# Revit family: 63 T Schraubflansch
name_source: partatom
category: Instalační zařizovací předměty
revit_build: Autodesk Revit 2016 (Build: 20161004_0715(x64)
units: mm (PartAtom-declared; Revit-internal decimal feet)

## family parameters
Bod výpočtu místnosti = Ano
Kóta kulaté spojky = Použít průměr
Nadpis OmniClass = Deck Waste Water Drains
Ořezat dutým tvarem při načtení = Ne
Sdílené = Ne
Typ součásti = Normální
Vždy vertikální = Ano
Založené na pracovní rovině = Ne
Číslo OmniClass = 23.70.50.21.24.14

## types (4) — shared parameters
BUILD-IN HEIGHT = 300 mm
Klíčová poznámka = 63 T Schraubflansch
MATERIAL = PP, TPE
Model = 63 T Schraubflansch
Popis = Roof drains
Připojení CW = Ne
Připojení HW = Ne
Připojení odpadu = Ano
Připojení ventilace = Ne
URL = http://www.dallmer.com
Výrobce = Dallmer Ltd.

## per-type parameters (varying)
| type | CAPACITY | DIMENSION | GTIN | Komentáře k typům | NOMINAL DIAMETER | WEIGHT |
| 63 T Schraubflansch.0049 | 9,7 | DN 70 | 4001636630049 | renova roof drain type 63 T clamp ring, 345 mm, DN 70 | 70 mm | 2,22 |
| 63 T Schraubflansch.0063 | 9,6 | DN 100 | 4001636630063 | renova roof drain type 63 T clamp ring, 460 mm, DN 100 | 100 mm | 2,75 |
| 63 T Schraubflansch.0087 | 14,2 | DN 125 | 4001636630087 | renova roof drain type 63 T clamp ring, 460 mm, DN 125 | 125 mm | 2,52 |
| 63 T Schraubflansch.0094 | 15 | DN 150 | 4001636630094 | renova roof drain type 63 T clamp ring, 345 mm, DN 150 | 150 mm | 2,86 |

## geometry (parser evidence)
native form markers: Sweep x3
no freeform markers — native parametric forms only
